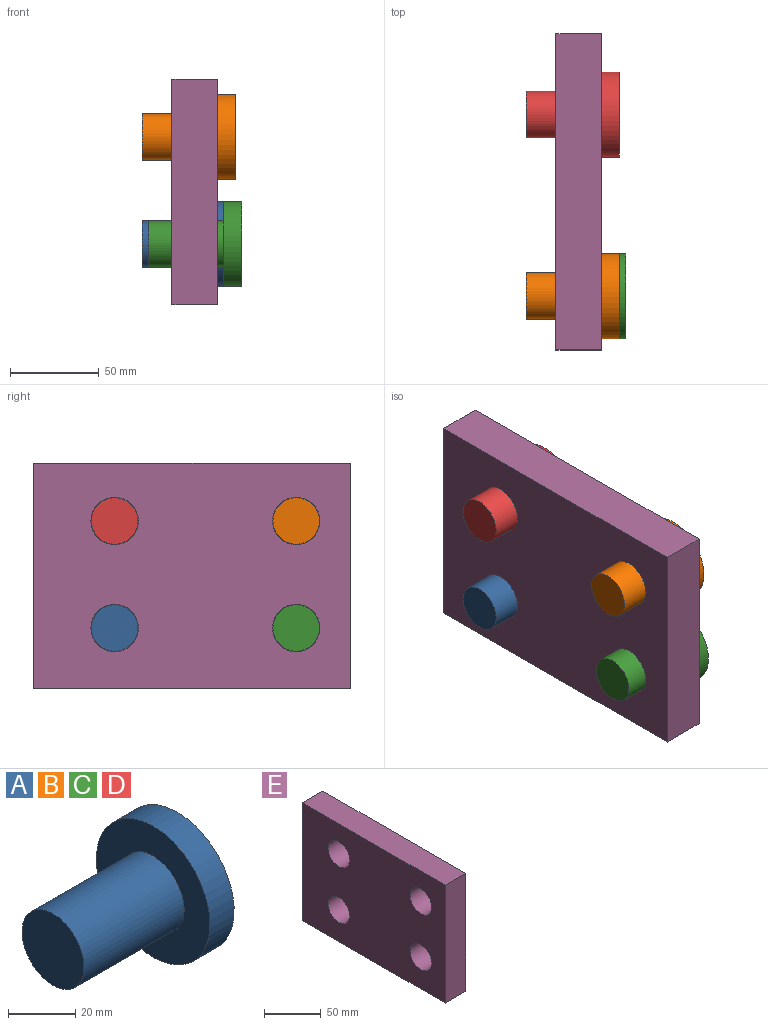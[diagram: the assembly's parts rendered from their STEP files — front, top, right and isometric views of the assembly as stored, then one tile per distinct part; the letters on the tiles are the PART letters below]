
ASSEMBLY  parts=5 mates=4
PART A: 5 faces, bbox 52.4x47.8x47.8 mm
  f0: plane 26.12x26.12mm, normal (-1,0,0), area 536mm2, adj f4
  f1: plane 47.8x47.8mm, normal (1,0,0), area 1794.4mm2, adj f2
  f2: cylinder r=23.9mm len=47.8mm, axis (1,0,0), area 1530.4mm2, adj f1,f3
  f3: plane 47.8x47.8mm, normal (-1,0,0), area 1258.4mm2, adj f2,f4
  f4: cylinder r=13.06mm len=42.16mm, axis (1,0,0), area 3460.2mm2, adj f0,f3
PART B: same geometry as A
PART C: same geometry as A
PART D: same geometry as A
PART E: 10 faces, bbox 25.4x177.8x127 mm
  f0: plane 177.8x25.4mm, normal (0,0,1), area 4516.1mm2, adj f1,f7,f8,f9
  f1: plane 127x25.4mm, normal (0,-1,0), area 3225.8mm2, adj f0,f2,f8,f9
  f2: plane 177.8x25.4mm, normal (0,0,-1), area 4516.1mm2, adj f1,f7,f8,f9
  f3: cylinder r=13.33mm len=26.67mm, axis (-1,0,0), area 2128.2mm2, adj f8,f9
  f4: cylinder r=13.33mm len=26.67mm, axis (-1,0,0), area 2128.2mm2, adj f8,f9
  f5: cylinder r=13.33mm len=26.67mm, axis (-1,0,0), area 2128.2mm2, adj f8,f9
  f6: cylinder r=13.33mm len=26.67mm, axis (-1,0,0), area 2128.2mm2, adj f8,f9
  f7: plane 127x25.4mm, normal (0,1,0), area 3225.8mm2, adj f0,f2,f8,f9
  f8: plane 177.8x127mm, normal (1,0,0), area 20346mm2, adj f0,f1,f2,f3,f4,f5,f6,f7
  f9: plane 177.8x127mm, normal (-1,0,0), area 20346mm2, adj f0,f1,f2,f3,f4,f5,f6,f7
PLACE A t=(0,102.05,-60.17)mm
PLACE B at identity
PLACE C t=(3.67,0,-60.17)mm
PLACE D t=(0,102.05,0)mm
PLACE E at identity fixed
MATE cylindrical C.f2 <-> E.f5  axis (1,0,0) through (29.07,-51.02,-60.17)mm
MATE fastened D.f2 <-> E.f3  axis (1,0,0) through (25.4,51.02,0)mm
MATE slider B.f2 <-> E.f6  axis (1,0,0) through (25.4,-51.02,0)mm
MATE fastened A.f2 <-> E.f4  axis (1,0,0) through (25.4,51.02,-60.17)mm
